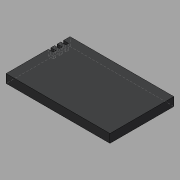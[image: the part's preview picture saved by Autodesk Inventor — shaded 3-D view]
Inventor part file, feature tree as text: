
AUTODESK INVENTOR PART (.ipt)
format: ipt  version: 2015 (Build 190159000, 159)  size: 96,256 bytes
history: native  units: mm
features: extrude x2, sketch x2
ambient origin geometry x8: Origin, YZ Plane, XZ Plane, XY Plane, X Axis, Y Axis, Z Axis, Center Point
bodies: Solid1 (feature_tree)
feature tree (4):
  extrude  "Extrusion1"  Depth=62.2mm
  extrude  "Extrusion2"  Depth=13.0mm
  sketch  "Sketch1"  dims[d0=38.3mm d1=62.2mm]
  sketch  "Sketch2"  dims[d2=5.1mm d3=0.0mm d4=13.0mm d5=3.0mm d6=3.9mm d7=1.6mm d8=2.2mm d9=1.6mm d10=2.2mm d11=3.6mm d12=0.0mm]
